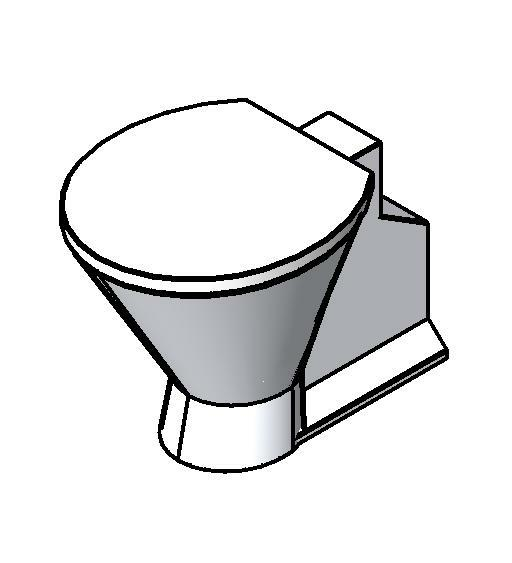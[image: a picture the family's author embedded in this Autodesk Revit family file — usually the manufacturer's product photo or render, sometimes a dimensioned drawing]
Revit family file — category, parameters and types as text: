
# Revit family: Deca_Acionamento torneira mesa redonda_Deca You_4991.104
name_source: partatom
category: Plumbing Fixtures
units: mm (PartAtom-declared; Revit-internal decimal feet)

## family parameters
Cut with Voids When Loaded = No
Host = Face
Part Type = Normal
Room Calculation Point = No
Round Connector Dimension = Use Radius
Shared = No

## types (11) — shared parameters
Acompanha o Produto = Mangueira Flexivel
Aprovado por = quattroD
Atendimento ao Cliente = 0800-0117073
Categoria = Acionamento Torneira Lavatório / Banheiro
Composição Básica = Liga de Cobre (Latão),Plásticos de Engenharia, Aço Inoxidavel e Elastômeros
Consumo = -
Cor Secundária = -
Criado por = quattroD
Itens de Instalação = -
Linha = Deca You
Manufacturer = DECA
Norma = Não possui
Pressão mín. Aquec. Acúmulo = -
Pressão mín. Aquec. Passagem = -
Saída de Esgoto = -
Segmento = Luxo
Tipo de dispositivo economizador = -
Tipo de mecanismo utilizado = MVC  - 1/4 de volta
Tipo de rosca de entrada = BSP
Tipo de rosca de saída = BSP
URL = www.deca.com.br
zero-valued in all types: CWFU, Default Elevation, Diâmetro Ponto de Esgoto, Diâmetro Água Fria, Peso Líquido (Kg), Raio Ponto de Esgoto, Raio Água Fria, WFU

## per-type parameters (varying)
| type | Cor Principal | Código Pai | Material | Model |
| 4991.C104_Cromado | Cromado | 4991.C104 | Deca_Cromado | 4991.C104 |
| 4991.BL104.MT_Black Matte | Black Matte | 4991.BL104.MT | Deca_Black Matte | 4991.BL104.MT |
| 4991.GF104.MT_Grafite | Antracite Dark | 4991.GF104.MT | Deca_Grafite | 4991.GF104.MT |
| 4991.INX104_Inox | Inox | 4991.INX104 | Deca_Inox | 4991.INX104 |
| 4991.MR104.MT_Brown Matte | BROWN MATTE | 4991.MR104.MT | Deca_Brown Matte | 4991.MR104.MT |
| 4991.SM104.MT_Summer Gold | SUMMER GOLD | 4991.SM104.MT | Deca_Summer Gold | 4991.SM104.MT |
| 4991.BR104.MT_Dynamic White | Dynamic White | 4991.BR104.MT | Deca_Dynamic White | 4991.BR104.MT |
| 4991.LS104.MT_Dynamic Gold | Dynamic Gold | 4991.LS104.MT | Deca_Dynamic Gold | 4991.LS104.MT |
| 4991.CL104.MT_Dynamic Peach | Dynamic Peach | 4991.CL104.MT | Deca_Dynamic Peach | 4991.CL104.MT |
| 4991.LV104.MT_Dynamic Lilac | Dynamic Lilac | 4991.LV104.MT | Deca_Dynamic Lilac | 4991.LV104.MT |
| 4991.AZ104.MT_Dynamic Blue | Dynamic Blue | 4991.AZ104.MT | Deca_Dynamic Blue | 4991.AZ104.MT |

## geometry (parser evidence)
native form markers: Sweep x2
no freeform markers — native parametric forms only
